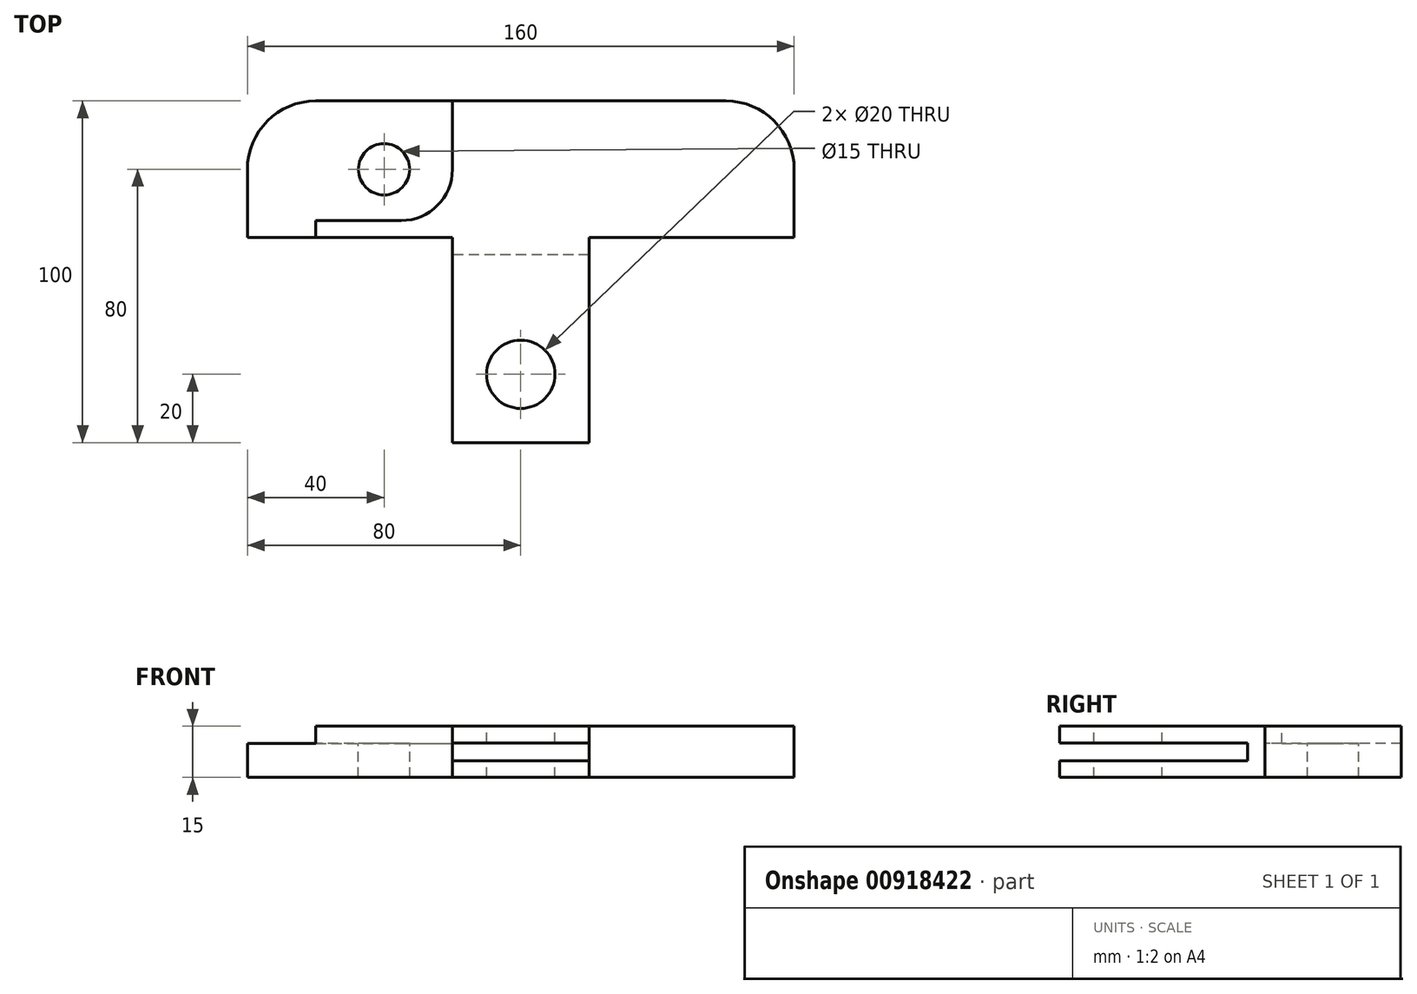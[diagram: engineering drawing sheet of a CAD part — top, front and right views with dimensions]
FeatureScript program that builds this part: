
annotation { "Feature Type Name" : "Feature", "Feature Type Description" : "" }
export const myFeature = defineFeature(function(context is Context, id is Id, definition is map)
    precondition{}
    {
        {
            var Q0;
            Q0=qCreatedBy(makeId("Top.planeOp"),FACE);
            var sketch = newSketch(context, id + "F0", { "sketchPlane" : qUnion([Q0])});
            skLineSegment(sketch, "E0", {"start": v(-115.23, 0) * mm, "end": v(121.54, 0) * mm, "construction": true});
            skLineSegment(sketch, "E1", {"start": v(0, 97) * mm, "end": v(0, -110.5) * mm, "construction": true});
            skLineSegment(sketch, "E2.0", {"start": v(-80, 20) * mm, "end": v(80, 20) * mm});
            skLineSegment(sketch, "E3.0", {"start": v(-80, 20) * mm, "end": v(-80, -80) * mm});
            skLineSegment(sketch, "E4.0", {"start": v(80, 20) * mm, "end": v(80, -80) * mm});
            skLineSegment(sketch, "E5.0", {"start": v(-80, -80) * mm, "end": v(80, -80) * mm});
            skLineSegment(sketch, "E6.filletArc", {"start": v(-80, 20) * mm, "end": v(-80, 20) * mm});
            skLineSegment(sketch, "E7.filletArc", {"start": v(-80, -80) * mm, "end": v(-80, -80) * mm});
            skLineSegment(sketch, "E8.filletArc", {"start": v(80, 20) * mm, "end": v(80, 20) * mm});
            skLineSegment(sketch, "E9.filletArc", {"start": v(80, -80) * mm, "end": v(80, -80) * mm});
            skSolve(sketch);
        }
        {
            var Q0;
            Q0=makeQuery(id+"F0.imprint","IMPRINT",FACE,{"disambiguationData":[TD([[makeQuery(id+"F0.imprint","IMPRINT",EDGE,{"derivedFrom":sQuery(id+"F0.wireOp",EDGE,"E2.0")}),-1.0]])]});
            extrude(context, id + "F1", {"entities" : qUnion([Q0]), "endBound" : BoundingType.SYMMETRIC, "depth" : 15 * mm, "offsetDistance" : 25 * mm});
        }
        {
            var Q0;
            Q0=qCreatedBy(makeId("Top.planeOp"),FACE);
            var sketch = newSketch(context, id + "F2", { "sketchPlane" : qUnion([Q0])});
            skLineSegment(sketch, "E10.bottom", {"start": v(-20, -20) * mm, "end": v(-80, -20) * mm});
            skLineSegment(sketch, "E10.top", {"start": v(-20, -80) * mm, "end": v(-80, -80) * mm});
            skLineSegment(sketch, "E10.left", {"start": v(-20, -20) * mm, "end": v(-20, -80) * mm});
            skLineSegment(sketch, "E10.right", {"start": v(-80, -20) * mm, "end": v(-80, -80) * mm});
            skLineSegment(sketch, "E11.MirrorCS", {"start": v(20, -20) * mm, "end": v(20, -80) * mm});
            skLineSegment(sketch, "E12.MirrorCS", {"start": v(20, -20) * mm, "end": v(80, -20) * mm});
            skLineSegment(sketch, "E13.MirrorCS", {"start": v(80, -20) * mm, "end": v(80, -80) * mm});
            skLineSegment(sketch, "E14.MirrorCS", {"start": v(20, -80) * mm, "end": v(80, -80) * mm});
            skSolve(sketch);
        }
        {
            var Q0;
            Q0 = qSketchRegion(id + "F2", true);
            extrude(context, id + "F3", {"entities" : qUnion([Q0]), "operationType" : NewBodyOperationType.REMOVE, "endBound" : BoundingType.SYMMETRIC, "oppositeDirection" : true, "depth" : 20 * mm, "offsetDistance" : 25 * mm});
        }
        {
            var Q0;
            Q0=makeQuery(id+"F3.boolean.opBoolean","COPY",EDGE,{"derivedFrom":makeQuery(id+"F3.opExtrude","SWEPT_EDGE",EDGE,{"disambiguationData":[OSD([sQuery(id+"F2.wireOp",EDGE,"E11.MirrorCS"),sQuery(id+"F2.wireOp",EDGE,"E14.MirrorCS")])]})});
            var Q1;
            Q1=makeQuery(id+"F3.boolean.opBoolean","COPY",EDGE,{"derivedFrom":makeQuery(id+"F3.opExtrude","SWEPT_EDGE",EDGE,{"disambiguationData":[OSD([sQuery(id+"F2.wireOp",EDGE,"E10.top"),sQuery(id+"F2.wireOp",EDGE,"E10.left")])]})});
            var Q2;
            Q2=makeQuery(id+"F3.boolean.opBoolean","COPY",EDGE,{"derivedFrom":makeQuery(id+"F3.opExtrude","SWEPT_EDGE",EDGE,{"disambiguationData":[OSD([sQuery(id+"F2.wireOp",EDGE,"E12.MirrorCS"),sQuery(id+"F2.wireOp",EDGE,"E13.MirrorCS")])]})});
            var Q3;
            Q3=makeQuery(id+"F1.opExtrude","SWEPT_EDGE",EDGE,{"disambiguationData":[OSD([sQuery(id+"F0.wireOp",EDGE,"E2.0"),sQuery(id+"F0.wireOp",EDGE,"E4.0")])]});
            var Q4;
            Q4=makeQuery(id+"F3.boolean.opBoolean","COPY",EDGE,{"derivedFrom":makeQuery(id+"F3.opExtrude","SWEPT_EDGE",EDGE,{"disambiguationData":[OSD([sQuery(id+"F2.wireOp",EDGE,"E10.bottom"),sQuery(id+"F2.wireOp",EDGE,"E10.right")])]})});
            var Q5;
            Q5=makeQuery(id+"F1.opExtrude","SWEPT_EDGE",EDGE,{"disambiguationData":[OSD([sQuery(id+"F0.wireOp",EDGE,"E2.0"),sQuery(id+"F0.wireOp",EDGE,"E3.0")])]});
            fillet(context, id + "F4", {"entities" : qUnion([Q0, Q1, Q2, Q3, Q4, Q5]), "radius" : 20 * mm, "tangentPropagation" : true, "allowEdgeOverflow" : false});
        }
        {
            var Q0;
            Q0=qCreatedBy(makeId("Right.planeOp"),FACE);
            var sketch = newSketch(context, id + "F5", { "sketchPlane" : qUnion([Q0])});
            skLineSegment(sketch, "E15", {"start": v(0, 32.38) * mm, "end": v(0, -44.55) * mm, "construction": true});
            skLineSegment(sketch, "E16.bottom", {"start": v(-82.34, 2.59) * mm, "end": v(-25, 2.59) * mm});
            skLineSegment(sketch, "E16.top", {"start": v(-82.34, -2.59) * mm, "end": v(-25, -2.59) * mm});
            skLineSegment(sketch, "E16.left", {"start": v(-82.34, 2.59) * mm, "end": v(-82.34, -2.59) * mm});
            skLineSegment(sketch, "E16.right", {"start": v(-25, 2.59) * mm, "end": v(-25, -2.59) * mm});
            skSolve(sketch);
        }
        {
            var Q0;
            Q0=makeQuery(id+"F5.imprint","IMPRINT",FACE,{"disambiguationData":[TD([[makeQuery(id+"F5.imprint","IMPRINT",EDGE,{"derivedFrom":sQuery(id+"F5.wireOp",EDGE,"E16.bottom")}),-1.0]])]});
            extrude(context, id + "F6", {"entities" : qUnion([Q0]), "operationType" : NewBodyOperationType.REMOVE, "endBound" : BoundingType.SYMMETRIC, "depth" : 50 * mm, "offsetDistance" : 25 * mm});
        }
        {
            var Q0;
            Q0=makeQuery(id+"F1.opExtrude","CAP_FACE",FACE,{"disambiguationData":[OSD([sQuery(id+"F0.wireOp",EDGE,"E2.0"),sQuery(id+"F0.wireOp",EDGE,"E3.0"),sQuery(id+"F0.wireOp",EDGE,"E4.0"),sQuery(id+"F0.wireOp",EDGE,"E5.0")])],"isStart":false});
            var sketch = newSketch(context, id + "F7", { "sketchPlane" : qUnion([Q0])});
            skLineSegment(sketch, "E17", {"start": v(-119.51, 0) * mm, "end": v(134.9, 0) * mm, "construction": true});
            skLineSegment(sketch, "E18", {"start": v(0, 72.2) * mm, "end": v(0, -122.48) * mm, "construction": true});
            skLineSegment(sketch, "E19.0", {"start": v(-20, 29.16) * mm, "end": v(-20, -15) * mm});
            skLineSegment(sketch, "E20.0", {"start": v(-20, -15) * mm, "end": v(-60, -15) * mm});
            skLineSegment(sketch, "E21.0", {"start": v(-60, -15) * mm, "end": v(-60, -35.4) * mm});
            skLineSegment(sketch, "E22.filletArc", {"start": v(-60, -15) * mm, "end": v(-60, -15) * mm});
            skLineSegment(sketch, "E23", {"start": v(-20, 29.16) * mm, "end": v(-92.19, 29.16) * mm});
            skLineSegment(sketch, "E24", {"start": v(-92.19, 29.16) * mm, "end": v(-92.19, -35.4) * mm});
            skLineSegment(sketch, "E25", {"start": v(-92.19, -35.4) * mm, "end": v(-60, -35.4) * mm});
            skLineSegment(sketch, "E26.filletArc", {"start": v(-20, 29.16) * mm, "end": v(-20, 29.16) * mm});
            skLineSegment(sketch, "E27.filletArc", {"start": v(-60, -35.4) * mm, "end": v(-60, -35.4) * mm});
            skSolve(sketch);
        }
        {
            var Q0;
            {var subQ5=sQuery(id+"F7.wireOp",EDGE,"E20.0");Q0=makeQuery(id+"F7.imprint","IMPRINT",FACE,{"disambiguationData":[TD([[makeQuery(id+"F7.imprint","IMPRINT",EDGE,{"derivedFrom":subQ5}),-1.0]])]});}
            extrude(context, id + "F8", {"entities" : qUnion([Q0]), "operationType" : NewBodyOperationType.REMOVE, "oppositeDirection" : true, "depth" : 5 * mm, "offsetDistance" : 25 * mm});
        }
        {
            var Q0;
            Q0=makeQuery(id+"F8.boolean.opBoolean","COPY",EDGE,{"derivedFrom":makeQuery(id+"F8.opExtrude","SWEPT_EDGE",EDGE,{"disambiguationData":[OSD([sQuery(id+"F7.wireOp",EDGE,"E19.0"),sQuery(id+"F7.wireOp",EDGE,"E20.0")])]})});
            fillet(context, id + "F9", {"entities" : qUnion([Q0]), "radius" : 15 * mm, "tangentPropagation" : true, "allowEdgeOverflow" : false});
        }
        {
            var Q0;
            Q0=makeQuery(id+"F8.boolean.opBoolean","COPY",FACE,{"derivedFrom":makeQuery(id+"F8.opExtrude","CAP_FACE",FACE,{"disambiguationData":[OSD([sQuery(id+"F0.wireOp",EDGE,"E2.0"),sQuery(id+"F0.wireOp",EDGE,"E3.0"),sQuery(id+"F0.wireOp",EDGE,"E4.0"),sQuery(id+"F0.wireOp",EDGE,"E5.0"),sQuery(id+"F7.wireOp",EDGE,"E19.0"),sQuery(id+"F7.wireOp",EDGE,"E20.0"),sQuery(id+"F7.wireOp",EDGE,"E21.0")])],"isStart":false})});
            var sketch = newSketch(context, id + "F10", { "sketchPlane" : qUnion([Q0])});
            skLineSegment(sketch, "E28", {"start": v(0, 50.49) * mm, "end": v(0, -87.77) * mm, "construction": true});
            skLineSegment(sketch, "E29", {"start": v(-91.74, 0) * mm, "end": v(92.9, 0) * mm, "construction": true});
            skLineSegment(sketch, "E30.0", {"start": v(-40, 50.49) * mm, "end": v(-40, -87.77) * mm, "construction": true});
            skCircle(sketch, "E31", {"center": v(-40, 0) * mm, "radius": 7.5 * mm});
            skSolve(sketch);
        }
        {
            var Q0;
            Q0=makeQuery(id+"F10.imprint","IMPRINT",FACE,{"disambiguationData":[TD([[makeQuery(id+"F10.imprint","IMPRINT",EDGE,{"derivedFrom":sQuery(id+"F10.wireOp",EDGE,"E31")}),1.0]])]});
            extrude(context, id + "F11", {"entities" : qUnion([Q0]), "operationType" : NewBodyOperationType.REMOVE, "endBound" : BoundingType.THROUGH_ALL, "oppositeDirection" : true, "depth" : 25 * mm, "offsetDistance" : 25 * mm});
        }
        {
            var Q0;
            Q0=makeQuery(id+"F1.opExtrude","CAP_FACE",FACE,{"disambiguationData":[OSD([sQuery(id+"F0.wireOp",EDGE,"E2.0"),sQuery(id+"F0.wireOp",EDGE,"E3.0"),sQuery(id+"F0.wireOp",EDGE,"E4.0"),sQuery(id+"F0.wireOp",EDGE,"E5.0")])],"isStart":false});
            var sketch = newSketch(context, id + "F12", { "sketchPlane" : qUnion([Q0])});
            skLineSegment(sketch, "E32.0", {"start": v(-20, -60) * mm, "end": v(20, -60) * mm, "construction": true});
            skLineSegment(sketch, "E33", {"start": v(0, 29.1) * mm, "end": v(0, -93.54) * mm, "construction": true});
            skPoint(sketch, "E33.startSnap0", {"position": v(0, 20) * mm});
            skCircle(sketch, "E34", {"center": v(0, -60) * mm, "radius": 10 * mm});
            skSolve(sketch);
        }
        {
            var Q0;
            Q0=makeQuery(id+"F12.imprint","IMPRINT",FACE,{"disambiguationData":[TD([[makeQuery(id+"F12.imprint","IMPRINT",EDGE,{"derivedFrom":sQuery(id+"F12.wireOp",EDGE,"E34")}),1.0]])]});
            extrude(context, id + "F13", {"entities" : qUnion([Q0]), "operationType" : NewBodyOperationType.REMOVE, "endBound" : BoundingType.THROUGH_ALL, "oppositeDirection" : true, "depth" : 25 * mm, "offsetDistance" : 25 * mm});
        }
    });
